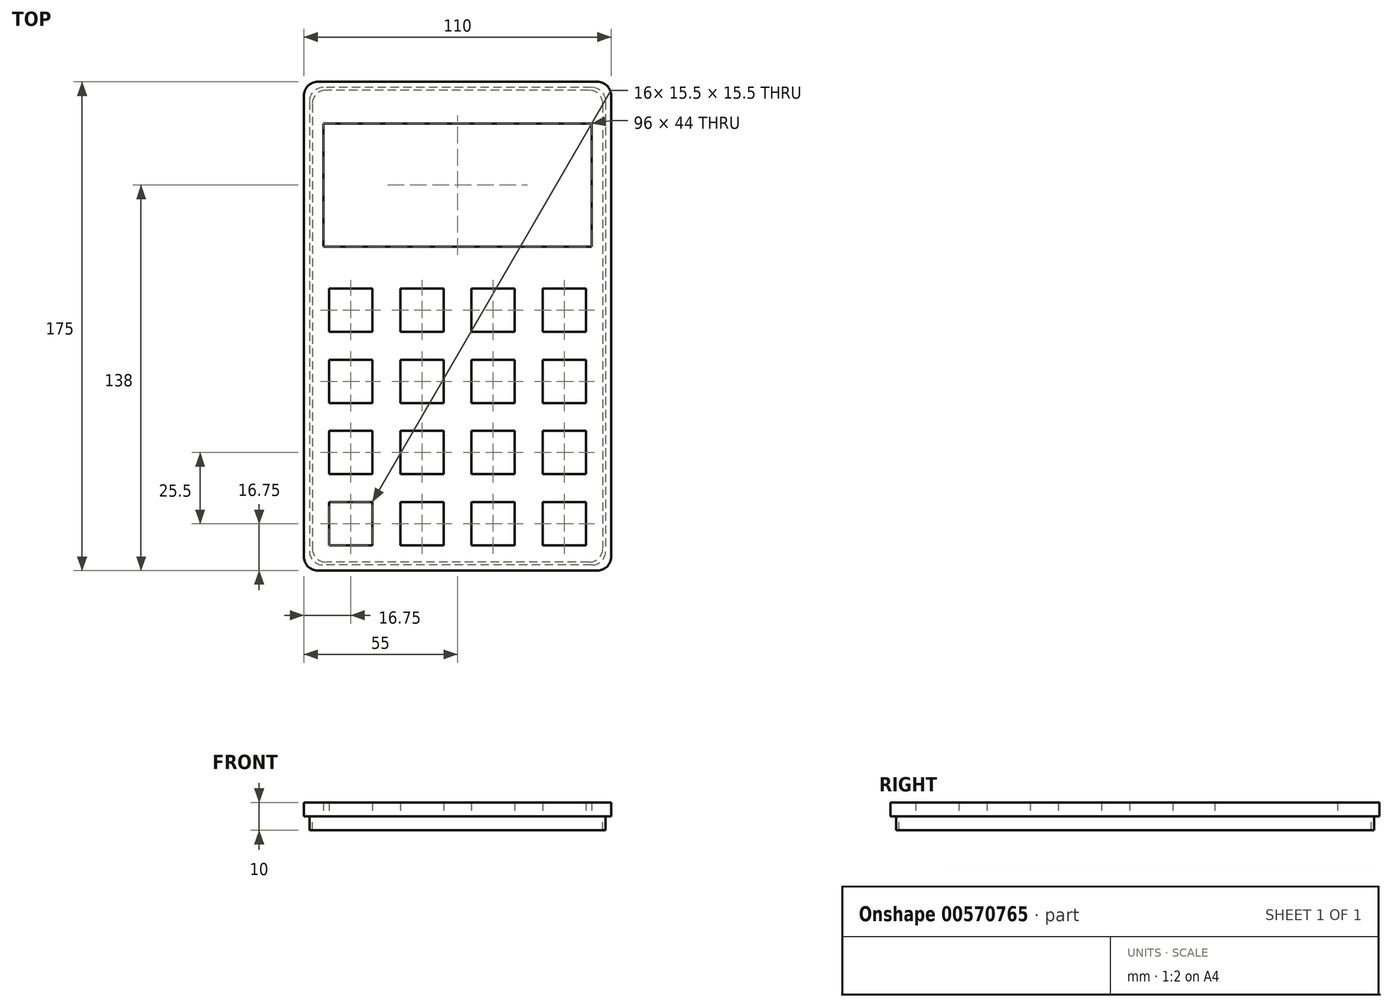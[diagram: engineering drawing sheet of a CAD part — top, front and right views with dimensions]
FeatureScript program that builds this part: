
annotation { "Feature Type Name" : "Feature", "Feature Type Description" : "" }
export const myFeature = defineFeature(function(context is Context, id is Id, definition is map)
    precondition{}
    {
        {
            var Q0;
            Q0=qCreatedBy(makeId("Top.planeOp"),FACE);
            var sketch = newSketch(context, id + "F0", { "sketchPlane" : qUnion([Q0])});
            skLineSegment(sketch, "E0.bottom", {"start": v(5, 0) * mm, "end": v(105, 0) * mm});
            skLineSegment(sketch, "E0.top", {"start": v(5, 175) * mm, "end": v(105, 175) * mm});
            skLineSegment(sketch, "E0.left", {"start": v(0, 5) * mm, "end": v(0, 170) * mm});
            skLineSegment(sketch, "E0.right", {"start": v(110, 5) * mm, "end": v(110, 170) * mm});
            skLineSegment(sketch, "E1.bottom", {"start": v(9, 24.5) * mm, "end": v(24.5, 24.5) * mm});
            skLineSegment(sketch, "E1.top", {"start": v(9, 9) * mm, "end": v(24.5, 9) * mm});
            skLineSegment(sketch, "E1.left", {"start": v(9, 24.5) * mm, "end": v(9, 9) * mm});
            skLineSegment(sketch, "E1.right", {"start": v(24.5, 24.5) * mm, "end": v(24.5, 9) * mm});
            skLineSegment(sketch, "E2.0.1.0", {"start": v(9, 50) * mm, "end": v(24.5, 50) * mm});
            skLineSegment(sketch, "E2.0.1.1", {"start": v(24.5, 50) * mm, "end": v(24.5, 34.5) * mm});
            skLineSegment(sketch, "E2.0.1.2", {"start": v(9, 50) * mm, "end": v(9, 34.5) * mm});
            skLineSegment(sketch, "E2.0.1.3", {"start": v(9, 34.5) * mm, "end": v(24.5, 34.5) * mm});
            skLineSegment(sketch, "E2.0.2.0", {"start": v(9, 75.5) * mm, "end": v(24.5, 75.5) * mm});
            skLineSegment(sketch, "E2.0.2.1", {"start": v(24.5, 75.5) * mm, "end": v(24.5, 60) * mm});
            skLineSegment(sketch, "E2.0.2.2", {"start": v(9, 75.5) * mm, "end": v(9, 60) * mm});
            skLineSegment(sketch, "E2.0.2.3", {"start": v(9, 60) * mm, "end": v(24.5, 60) * mm});
            skLineSegment(sketch, "E2.0.3.0", {"start": v(9, 101) * mm, "end": v(24.5, 101) * mm});
            skLineSegment(sketch, "E2.0.3.1", {"start": v(24.5, 101) * mm, "end": v(24.5, 85.5) * mm});
            skLineSegment(sketch, "E2.0.3.2", {"start": v(9, 101) * mm, "end": v(9, 85.5) * mm});
            skLineSegment(sketch, "E2.0.3.3", {"start": v(9, 85.5) * mm, "end": v(24.5, 85.5) * mm});
            skLineSegment(sketch, "E2.1.0.0", {"start": v(34.5, 24.5) * mm, "end": v(50, 24.5) * mm});
            skLineSegment(sketch, "E2.1.0.1", {"start": v(50, 24.5) * mm, "end": v(50, 9) * mm});
            skLineSegment(sketch, "E2.1.0.2", {"start": v(34.5, 24.5) * mm, "end": v(34.5, 9) * mm});
            skLineSegment(sketch, "E2.1.0.3", {"start": v(34.5, 9) * mm, "end": v(50, 9) * mm});
            skLineSegment(sketch, "E2.1.1.0", {"start": v(34.5, 50) * mm, "end": v(50, 50) * mm});
            skLineSegment(sketch, "E2.1.1.1", {"start": v(50, 50) * mm, "end": v(50, 34.5) * mm});
            skLineSegment(sketch, "E2.1.1.2", {"start": v(34.5, 50) * mm, "end": v(34.5, 34.5) * mm});
            skLineSegment(sketch, "E2.1.1.3", {"start": v(34.5, 34.5) * mm, "end": v(50, 34.5) * mm});
            skLineSegment(sketch, "E2.1.2.0", {"start": v(34.5, 75.5) * mm, "end": v(50, 75.5) * mm});
            skLineSegment(sketch, "E2.1.2.1", {"start": v(50, 75.5) * mm, "end": v(50, 60) * mm});
            skLineSegment(sketch, "E2.1.2.2", {"start": v(34.5, 75.5) * mm, "end": v(34.5, 60) * mm});
            skLineSegment(sketch, "E2.1.2.3", {"start": v(34.5, 60) * mm, "end": v(50, 60) * mm});
            skLineSegment(sketch, "E2.1.3.0", {"start": v(34.5, 101) * mm, "end": v(50, 101) * mm});
            skLineSegment(sketch, "E2.1.3.1", {"start": v(50, 101) * mm, "end": v(50, 85.5) * mm});
            skLineSegment(sketch, "E2.1.3.2", {"start": v(34.5, 101) * mm, "end": v(34.5, 85.5) * mm});
            skLineSegment(sketch, "E2.1.3.3", {"start": v(34.5, 85.5) * mm, "end": v(50, 85.5) * mm});
            skLineSegment(sketch, "E2.2.0.0", {"start": v(60, 24.5) * mm, "end": v(75.5, 24.5) * mm});
            skLineSegment(sketch, "E2.2.0.1", {"start": v(75.5, 24.5) * mm, "end": v(75.5, 9) * mm});
            skLineSegment(sketch, "E2.2.0.2", {"start": v(60, 24.5) * mm, "end": v(60, 9) * mm});
            skLineSegment(sketch, "E2.2.0.3", {"start": v(60, 9) * mm, "end": v(75.5, 9) * mm});
            skLineSegment(sketch, "E2.2.1.0", {"start": v(60, 50) * mm, "end": v(75.5, 50) * mm});
            skLineSegment(sketch, "E2.2.1.1", {"start": v(75.5, 50) * mm, "end": v(75.5, 34.5) * mm});
            skLineSegment(sketch, "E2.2.1.2", {"start": v(60, 50) * mm, "end": v(60, 34.5) * mm});
            skLineSegment(sketch, "E2.2.1.3", {"start": v(60, 34.5) * mm, "end": v(75.5, 34.5) * mm});
            skLineSegment(sketch, "E2.2.2.0", {"start": v(60, 75.5) * mm, "end": v(75.5, 75.5) * mm});
            skLineSegment(sketch, "E2.2.2.1", {"start": v(75.5, 75.5) * mm, "end": v(75.5, 60) * mm});
            skLineSegment(sketch, "E2.2.2.2", {"start": v(60, 75.5) * mm, "end": v(60, 60) * mm});
            skLineSegment(sketch, "E2.2.2.3", {"start": v(60, 60) * mm, "end": v(75.5, 60) * mm});
            skLineSegment(sketch, "E2.2.3.0", {"start": v(60, 101) * mm, "end": v(75.5, 101) * mm});
            skLineSegment(sketch, "E2.2.3.1", {"start": v(75.5, 101) * mm, "end": v(75.5, 85.5) * mm});
            skLineSegment(sketch, "E2.2.3.2", {"start": v(60, 101) * mm, "end": v(60, 85.5) * mm});
            skLineSegment(sketch, "E2.2.3.3", {"start": v(60, 85.5) * mm, "end": v(75.5, 85.5) * mm});
            skLineSegment(sketch, "E2.3.0.0", {"start": v(85.5, 24.5) * mm, "end": v(101, 24.5) * mm});
            skLineSegment(sketch, "E2.3.0.1", {"start": v(101, 24.5) * mm, "end": v(101, 9) * mm});
            skLineSegment(sketch, "E2.3.0.2", {"start": v(85.5, 24.5) * mm, "end": v(85.5, 9) * mm});
            skLineSegment(sketch, "E2.3.0.3", {"start": v(85.5, 9) * mm, "end": v(101, 9) * mm});
            skLineSegment(sketch, "E2.3.1.0", {"start": v(85.5, 50) * mm, "end": v(101, 50) * mm});
            skLineSegment(sketch, "E2.3.1.1", {"start": v(101, 50) * mm, "end": v(101, 34.5) * mm});
            skLineSegment(sketch, "E2.3.1.2", {"start": v(85.5, 50) * mm, "end": v(85.5, 34.5) * mm});
            skLineSegment(sketch, "E2.3.1.3", {"start": v(85.5, 34.5) * mm, "end": v(101, 34.5) * mm});
            skLineSegment(sketch, "E2.3.2.0", {"start": v(85.5, 75.5) * mm, "end": v(101, 75.5) * mm});
            skLineSegment(sketch, "E2.3.2.1", {"start": v(101, 75.5) * mm, "end": v(101, 60) * mm});
            skLineSegment(sketch, "E2.3.2.2", {"start": v(85.5, 75.5) * mm, "end": v(85.5, 60) * mm});
            skLineSegment(sketch, "E2.3.2.3", {"start": v(85.5, 60) * mm, "end": v(101, 60) * mm});
            skLineSegment(sketch, "E2.3.3.0", {"start": v(85.5, 101) * mm, "end": v(101, 101) * mm});
            skLineSegment(sketch, "E2.3.3.1", {"start": v(101, 101) * mm, "end": v(101, 85.5) * mm});
            skLineSegment(sketch, "E2.3.3.2", {"start": v(85.5, 101) * mm, "end": v(85.5, 85.5) * mm});
            skLineSegment(sketch, "E2.3.3.3", {"start": v(85.5, 85.5) * mm, "end": v(101, 85.5) * mm});
            skLineSegment(sketch, "E2.direction1", {"start": v(9, 9) * mm, "end": v(34.5, 9) * mm, "construction": true});
            skLineSegment(sketch, "E2.direction2", {"start": v(9, 9) * mm, "end": v(9, 34.5) * mm, "construction": true});
            skLineSegment(sketch, "E3.bottom", {"start": v(7, 116) * mm, "end": v(103, 116) * mm});
            skLineSegment(sketch, "E3.top", {"start": v(7, 160) * mm, "end": v(103, 160) * mm});
            skLineSegment(sketch, "E3.left", {"start": v(7, 116) * mm, "end": v(7, 160) * mm});
            skLineSegment(sketch, "E3.right", {"start": v(103, 116) * mm, "end": v(103, 160) * mm});
            skPoint(sketch, "E4.visualSharp", {"position": v(0, 0) * mm});
            skArc(sketch, "E4.filletArc", {"start": v(0, 5) * mm, "mid": v(1.46, 1.46) * mm, "end": v(5, 0) * mm});
            skPoint(sketch, "E5.visualSharp", {"position": v(110, 0) * mm});
            skArc(sketch, "E5.filletArc", {"start": v(105, 0) * mm, "mid": v(108.54, 1.46) * mm, "end": v(110, 5) * mm});
            skPoint(sketch, "E6.visualSharp", {"position": v(110, 175) * mm});
            skArc(sketch, "E6.filletArc", {"start": v(110, 170) * mm, "mid": v(108.54, 173.54) * mm, "end": v(105, 175) * mm});
            skPoint(sketch, "E7.visualSharp", {"position": v(0, 175) * mm});
            skArc(sketch, "E7.filletArc", {"start": v(5, 175) * mm, "mid": v(1.46, 173.54) * mm, "end": v(0, 170) * mm});
            skSolve(sketch);
        }
        {
            var Q0;
            Q0=makeQuery(id+"F0.imprint","IMPRINT",FACE,{"disambiguationData":[TD([[makeQuery(id+"F0.imprint","IMPRINT",EDGE,{"derivedFrom":sQuery(id+"F0.wireOp",EDGE,"E0.bottom")}),1.0]])]});
            extrude(context, id + "F1", {"entities" : qUnion([Q0]), "depth" : 5 * mm, "offsetDistance" : 25 * mm});
        }
        {
            var Q0;
            Q0=makeQuery(id+"F0.imprint","IMPRINT",FACE,{"disambiguationData":[TD([[makeQuery(id+"F0.imprint","IMPRINT",EDGE,{"derivedFrom":sQuery(id+"F0.wireOp",EDGE,"E0.bottom")}),1.0]])]});
            var sketch = newSketch(context, id + "F2", { "sketchPlane" : qUnion([Q0])});
            skLineSegment(sketch, "E8.bottom", {"start": v(103, 173) * mm, "end": v(7, 173) * mm});
            skLineSegment(sketch, "E8.top", {"start": v(103, 2) * mm, "end": v(7, 2) * mm});
            skLineSegment(sketch, "E8.left", {"start": v(108, 168) * mm, "end": v(108, 7) * mm});
            skLineSegment(sketch, "E8.right", {"start": v(2, 168) * mm, "end": v(2, 7) * mm});
            skPoint(sketch, "E9.visualSharp", {"position": v(108, 2) * mm});
            skArc(sketch, "E9.filletArc", {"start": v(103, 2) * mm, "mid": v(106.54, 3.46) * mm, "end": v(108, 7) * mm});
            skPoint(sketch, "E10.visualSharp", {"position": v(2, 2) * mm});
            skArc(sketch, "E10.filletArc", {"start": v(2, 7) * mm, "mid": v(3.46, 3.46) * mm, "end": v(7, 2) * mm});
            skPoint(sketch, "E11.visualSharp", {"position": v(2, 173) * mm});
            skArc(sketch, "E11.filletArc", {"start": v(7, 173) * mm, "mid": v(3.46, 171.54) * mm, "end": v(2, 168) * mm});
            skPoint(sketch, "E12.visualSharp", {"position": v(108, 173) * mm});
            skArc(sketch, "E12.filletArc", {"start": v(108, 168) * mm, "mid": v(106.54, 171.54) * mm, "end": v(103, 173) * mm});
            skLineSegment(sketch, "E13.bottom", {"start": v(102, 172) * mm, "end": v(8, 172) * mm});
            skLineSegment(sketch, "E13.top", {"start": v(102, 3) * mm, "end": v(8, 3) * mm});
            skLineSegment(sketch, "E13.left", {"start": v(107, 167) * mm, "end": v(107, 8) * mm});
            skLineSegment(sketch, "E13.right", {"start": v(3, 167) * mm, "end": v(3, 8) * mm});
            skPoint(sketch, "E14.visualSharp", {"position": v(107, 172) * mm});
            skArc(sketch, "E14.filletArc", {"start": v(107, 167) * mm, "mid": v(105.54, 170.54) * mm, "end": v(102, 172) * mm});
            skPoint(sketch, "E15.visualSharp", {"position": v(3, 172) * mm});
            skArc(sketch, "E15.filletArc", {"start": v(8, 172) * mm, "mid": v(4.46, 170.54) * mm, "end": v(3, 167) * mm});
            skPoint(sketch, "E16.visualSharp", {"position": v(3, 3) * mm});
            skArc(sketch, "E16.filletArc", {"start": v(3, 8) * mm, "mid": v(4.46, 4.46) * mm, "end": v(8, 3) * mm});
            skPoint(sketch, "E17.visualSharp", {"position": v(107, 3) * mm});
            skArc(sketch, "E17.filletArc", {"start": v(102, 3) * mm, "mid": v(105.54, 4.46) * mm, "end": v(107, 8) * mm});
            skSolve(sketch);
        }
        {
            var Q0;
            Q0 = qSketchRegion(id + "F2", true);
            extrude(context, id + "F3", {"entities" : qUnion([Q0]), "operationType" : NewBodyOperationType.ADD, "oppositeDirection" : true, "depth" : 5 * mm, "offsetDistance" : 25 * mm});
        }
    });
